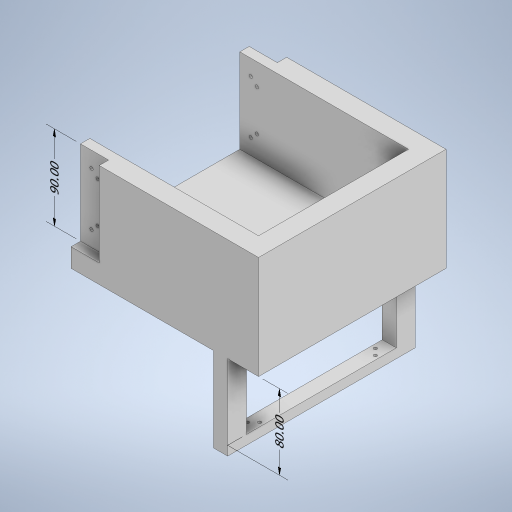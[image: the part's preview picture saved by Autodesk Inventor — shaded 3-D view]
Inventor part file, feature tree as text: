
AUTODESK INVENTOR PART (.ipt)
format: ipt  version: 2023 (Build 270158000, 158)  size: 335,360 bytes
history: native  units: mm
features: sketch x7, extrude x5, other x4, hole x2
ambient origin geometry x8: Origin, YZ Plane, XZ Plane, XY Plane, X Axis, Y Axis, Z Axis, Center Point
bodies: Body1 (feature_tree)
feature tree (18):
  other  "Sólido1"
  other  "Anotaciones"
  extrude  "Extrusión1"  Depth=200.0mm
  hole  "Agujero1"  [1 undecoded]
  extrude  "Extrusión2"  Depth=15.0mm
  extrude  "Extrusión3"  Depth=80.0mm TaperAngle=0.0deg
  extrude  "Extrusión4"  Depth=200.0mm
  extrude  "Extrusión5"  Depth=20.0mm
  hole  "Agujero2"  [1 undecoded]
  sketch  "Boceto2"  dims[d7=15.0mm d8=200.0mm]
  sketch  "Boceto3"  dims[d9=10.0mm d10=0.0mm]
  sketch  "Boceto4"  dims[d12=1.75mm d13=1.75mm d14=1.75mm d15=1.75mm d16=10.0mm d17=10.0mm d19=30.0mm]
  sketch  "Boceto5"  dims[d20=3.5mm d21=6.0mm d22=4.0mm d23=2.0mm d24=90.0deg d25=8.0mm d26=20.594885mm d27=15.0mm]
  sketch  "Boceto6"  dims[d28=20.0mm d29=80.0mm d30=0.0mm]
  sketch  "Boceto7"  dims[d31=48.0mm d32=200.0mm]
  sketch  "Boceto8"  dims[d33=110.0mm d34=0.0mm d36=20.0mm d37=20.0mm d38=20.0mm d39=90.0mm d40=0.0mm d42=10.0mm d43=30.0mm d44=0.0mm d46=1.75mm d47=1.75mm d48=1.75mm d49=1.75mm d50=10.0mm d51=10.0mm d52=15.0mm d56=3.5mm d57=6.0mm d58=4.0mm d59=2.0mm d60=90.0deg d61=8.0mm d62=20.594885mm d63=10.0mm d65=10.0mm d66=10.0mm d67=31.75mm d70=15.0mm d74=200.0mm d78=20.0mm d75=1.454734mm d76=6.982969mm d77=80.0mm d79=4.097996mm d80=1.406125mm d81=90.0mm]
  other  "Cota lineal 2"
  other  "Cota lineal 3"
note: 2 required parameter values undecoded (feature->parameter linkage not recoverable at this tier; creation-order binding heuristic only, values carry confidence <= 0.55)
